# Revit family: QF_LIEBHERR_GGPv 1490.191129125126
name_source: partatom
category: Specialty Equipment
revit_build: Autodesk Revit 2016 (Build: 20150220_1215(x64)
units: mm (PartAtom-declared; Revit-internal decimal feet)

## family parameters
Always vertical = Yes
Cut with Voids When Loaded = No
OmniClass Number = 23.40.40.14
OmniClass Title = Food Service Equipment
Part Type = Normal
Room Calculation Point = No
Round Connector Dimension = Use Diameter
Shared = No
Work Plane-Based = No

## types (1)
- GGPv 1490_230V/1Ph/50Hz
    Accessoires = No
    Consommation d'énergie minimale = 0 A
    Cost = 0 $
    Câble de connexion à l'appareil inclus = No
    Description = GN FREEZER GGPV 1490, -10/-26°C, S/STEEL EXTERIOR & INTERIOR, 1056 L NET
    Fréquence = 50 Hz
    Hauteur hors tout = 2120 mm  [stored 6.95538 ft]
    Intensité nominale courant electrique = 5 A
    Longueur hors tout = 1430 mm  [stored 4.6916 ft]
    Manufacturer = LIEBHERR
    Model = GGPv 1490
    Nombres de Pôles = 2
    Phase = 1
    Poids net à vide = 195.00 kg
    Profondeur hors tout = 830 mm  [stored 2.7231 ft]
    Protection de l'Appareil = 0 A
    Puissance Apparente = 450 VA
    Puissance électrique  = 450 W
    Tension = 230 V
    URL = home.liebherr.com

note: [stored X ft] marks values corroborated as IEEE doubles in the binary element streams (Revit-internal decimal feet)

## geometry (parser evidence)
native form markers: Sweep x5
no freeform markers — native parametric forms only
